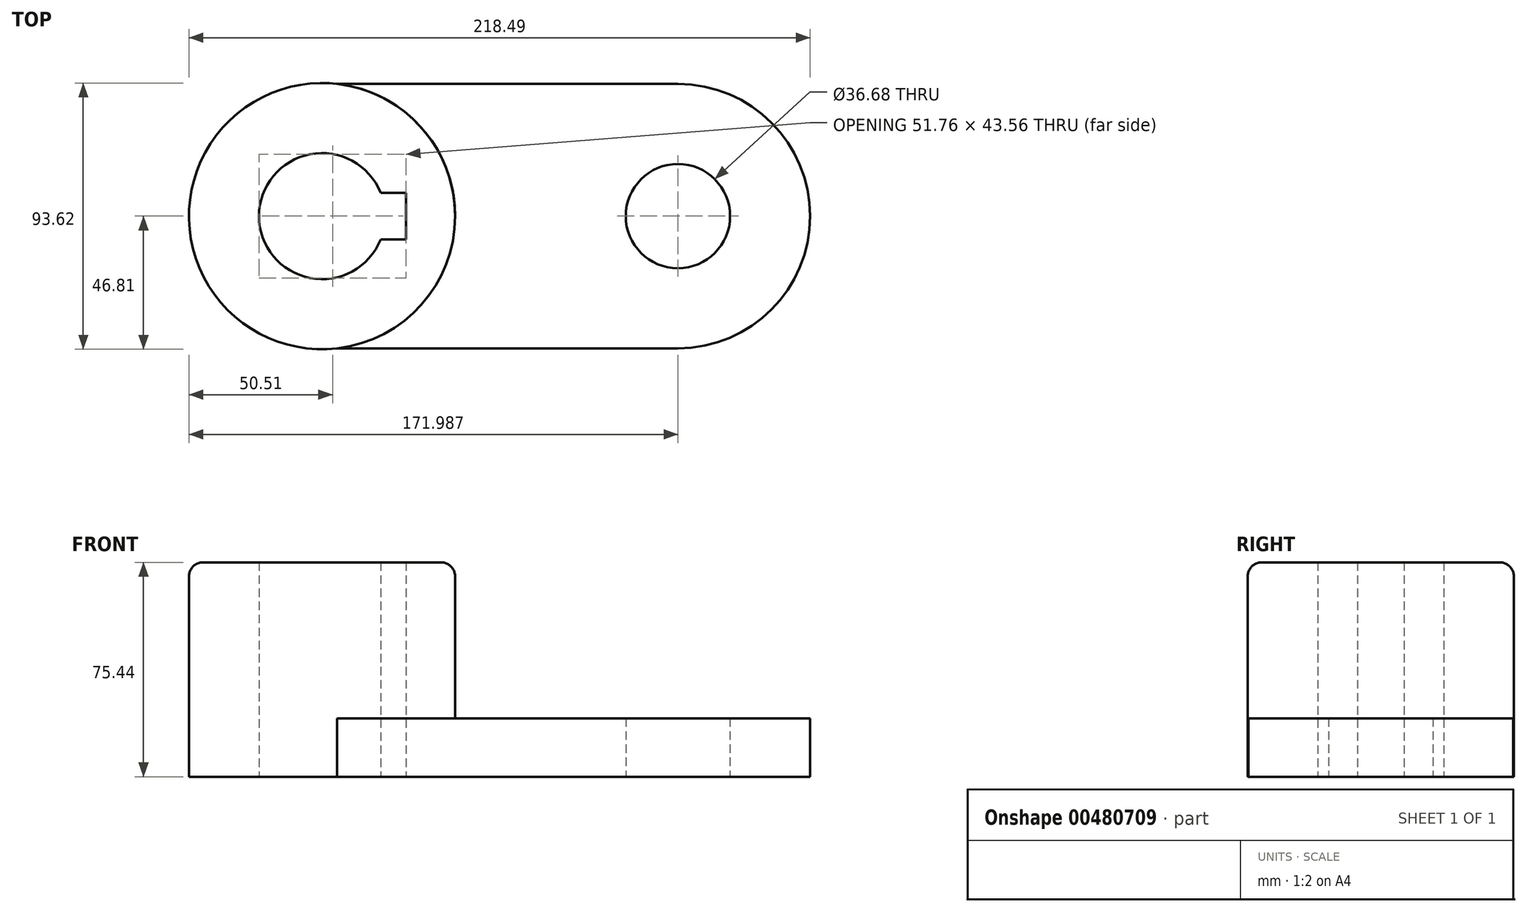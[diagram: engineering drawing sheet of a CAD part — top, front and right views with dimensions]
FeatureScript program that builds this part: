
annotation { "Feature Type Name" : "Feature", "Feature Type Description" : "" }
export const myFeature = defineFeature(function(context is Context, id is Id, definition is map)
    precondition{}
    {
        {
            var Q0;
            Q0=qCreatedBy(makeId("Top.planeOp"),FACE);
            var sketch = newSketch(context, id + "F0", { "sketchPlane" : qUnion([Q0])});
            skCircle(sketch, "E0", {"center": v(0, 0) * mm, "radius": 46.8 * mm});
            skLineSegment(sketch, "E1.bottom", {"start": v(-20.6, 8.23) * mm, "end": v(29.58, 8.23) * mm});
            skLineSegment(sketch, "E1.top", {"start": v(-20.6, -8.23) * mm, "end": v(29.58, -8.23) * mm});
            skLineSegment(sketch, "E1.right", {"start": v(29.58, 8.23) * mm, "end": v(29.58, -8.23) * mm});
            skCircle(sketch, "E2", {"center": v(125.18, 0) * mm, "radius": 18.34 * mm});
            skArc(sketch, "E3", {"start": v(125.18, -46.5) * mm, "mid": v(171.68, 0) * mm, "end": v(125.18, 46.5) * mm});
            skLineSegment(sketch, "E4", {"start": v(5.34, 46.5) * mm, "end": v(125.18, 46.5) * mm});
            skLineSegment(sketch, "E5", {"start": v(5.34, -46.5) * mm, "end": v(125.18, -46.5) * mm});
            skCircle(sketch, "E6", {"center": v(0, 0) * mm, "radius": 41.74 * mm});
            skCircle(sketch, "E7", {"center": v(0, 0) * mm, "radius": 22.18 * mm});
            skPoint(sketch, "E8.orphan", {"position": v(-29.58, 8.23) * mm});
            skPoint(sketch, "E9.orphan", {"position": v(-29.58, -8.23) * mm});
            skSolve(sketch);
        }
        {
            var Q0;
            {var subQ0=sQuery(id+"F0.wireOp",EDGE,"E1.right");Q0=makeQuery(id+"F0.imprint","IMPRINT",FACE,{"disambiguationData":[TD([[makeQuery(id+"F0.imprint","IMPRINT",EDGE,{"derivedFrom":subQ0}),1.0]])]});}
            var Q1;
            Q1=makeQuery(id+"F0.imprint","IMPRINT",FACE,{"disambiguationData":[TD([[makeQuery(id+"F0.imprint","IMPRINT",EDGE,{"derivedFrom":sQuery(id+"F0.wireOp",EDGE,"E6")}),-1.0]])]});
            extrude(context, id + "F1", {"entities" : qUnion([Q0, Q1]), "depth" : 75.44 * mm});
        }
        {
            var Q0;
            Q0=makeQuery(id+"F0.imprint","IMPRINT",FACE,{"disambiguationData":[TD([[makeQuery(id+"F0.imprint","IMPRINT",EDGE,{"derivedFrom":sQuery(id+"F0.wireOp",EDGE,"E2")}),-1.0]])]});
            var Q1;
            {var subQ0=sQuery(id+"F0.wireOp",EDGE,"E4");Q1=makeQuery(id+"F0.imprint","IMPRINT",FACE,{"disambiguationData":[TD([[makeQuery(id+"F0.imprint","IMPRINT",EDGE,{"derivedFrom":subQ0}),-1.0]])]});}
            extrude(context, id + "F2", {"entities" : qUnion([Q0, Q1]), "operationType" : NewBodyOperationType.ADD, "depth" : 20.57 * mm});
        }
        {
            var Q0;
            Q0=makeQuery(id+"F0.imprint","IMPRINT",FACE,{"disambiguationData":[TD([[makeQuery(id+"F0.imprint","IMPRINT",EDGE,{"derivedFrom":sQuery(id+"F0.wireOp",EDGE,"E6")}),-1.0]])]});
            extrude(context, id + "F3", {"entities" : qUnion([Q0]), "operationType" : NewBodyOperationType.ADD, "depth" : 73 * mm});
        }
        {
            var Q0;
            Q0=makeQuery(id+"F1.opExtrude","CAP_EDGE",EDGE,{"disambiguationData":[OSD([sQuery(id+"F0.wireOp",EDGE,"E0")])],"isStart":false});
            fillet(context, id + "F4", {"entities" : qUnion([Q0]), "radius" : 5 * mm, "tangentPropagation" : true, "allowEdgeOverflow" : false});
        }
    });
